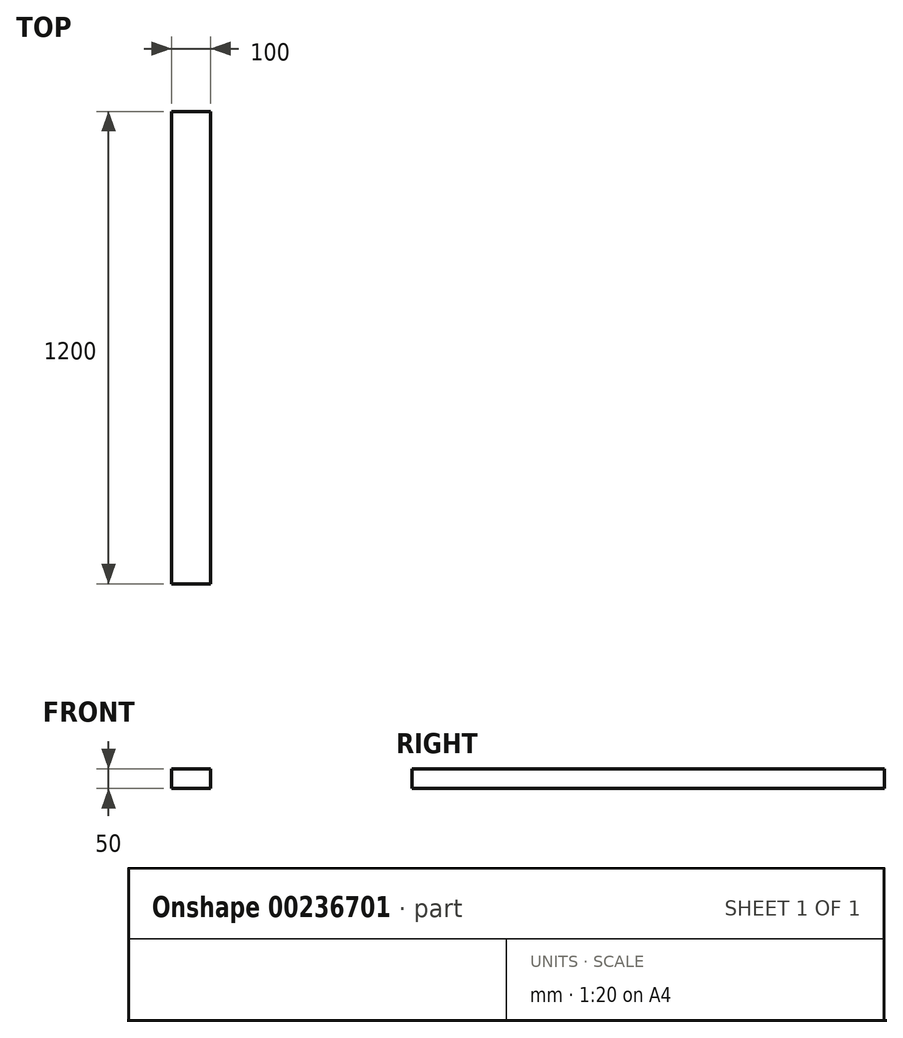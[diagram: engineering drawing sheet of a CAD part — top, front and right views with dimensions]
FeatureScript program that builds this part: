
annotation { "Feature Type Name" : "Feature", "Feature Type Description" : "" }
export const myFeature = defineFeature(function(context is Context, id is Id, definition is map)
    precondition{}
    {
        {
            var Q0;
            Q0=qCreatedBy(makeId("Front.planeOp"),FACE);
            var sketch = newSketch(context, id + "F0", { "sketchPlane" : qUnion([Q0])});
            skLineSegment(sketch, "E0.bottom", {"start": v(0, 0) * mm, "end": v(100, 0) * mm});
            skLineSegment(sketch, "E0.top", {"start": v(0, 50) * mm, "end": v(100, 50) * mm});
            skLineSegment(sketch, "E0.left", {"start": v(0, 0) * mm, "end": v(0, 50) * mm});
            skLineSegment(sketch, "E0.right", {"start": v(100, 0) * mm, "end": v(100, 50) * mm});
            skSolve(sketch);
        }
        {
            var Q0;
            Q0 = qSketchRegion(id + "F0", true);
            extrude(context, id + "F1", {"entities" : qUnion([Q0]), "depth" : 1200 * mm, "offsetDistance" : 25 * mm});
        }
    });
